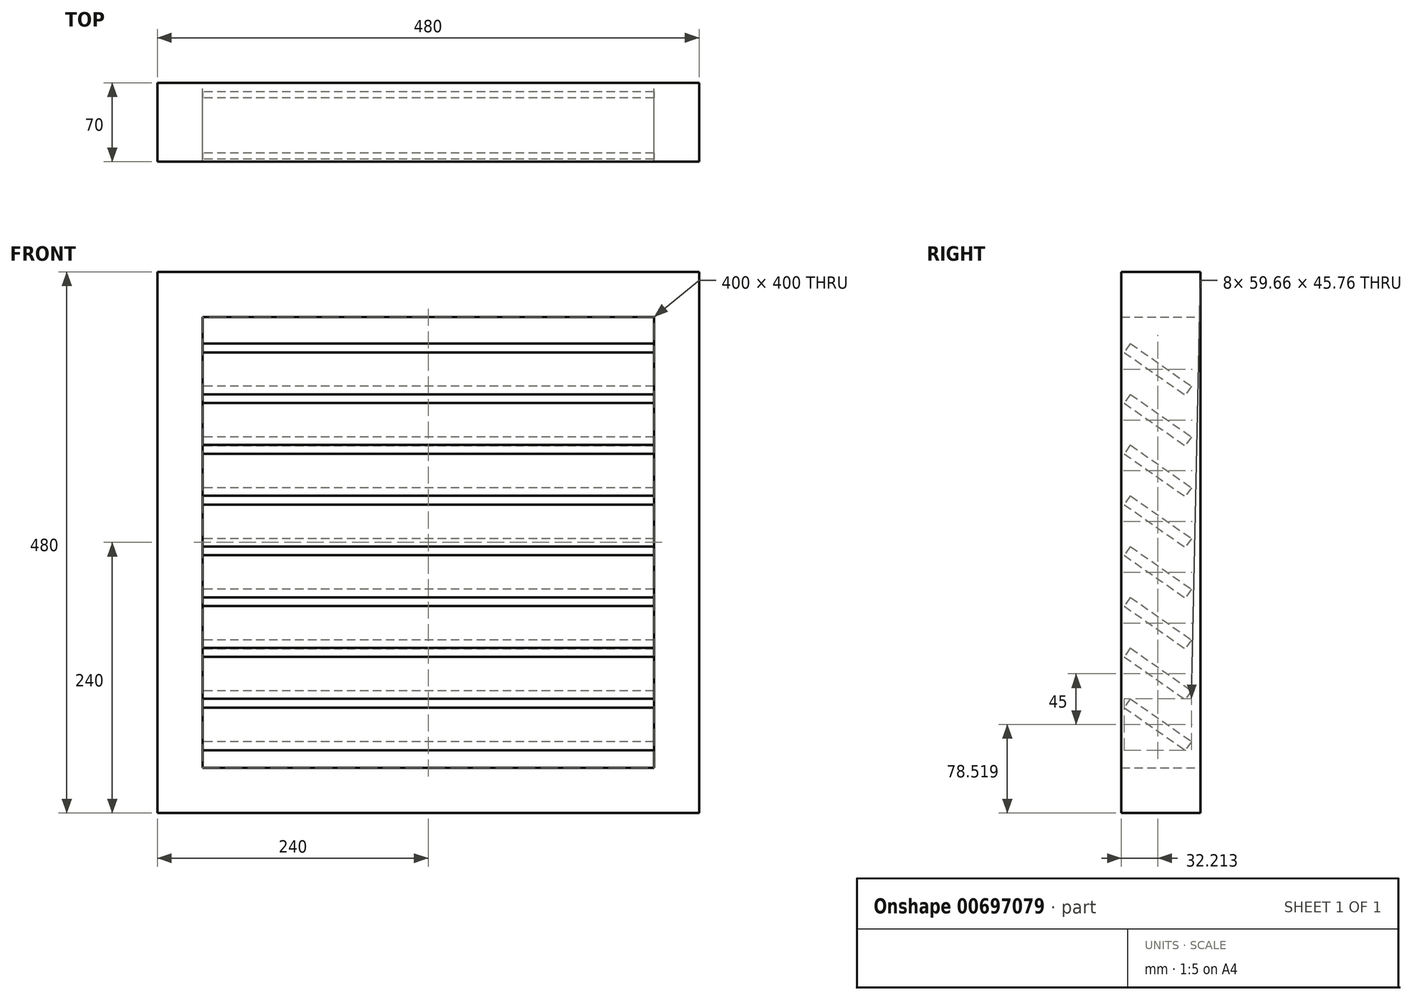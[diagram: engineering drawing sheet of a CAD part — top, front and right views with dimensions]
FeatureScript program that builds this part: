
annotation { "Feature Type Name" : "Feature", "Feature Type Description" : "" }
export const myFeature = defineFeature(function(context is Context, id is Id, definition is map)
    precondition{}
    {
        {
            var Q0;
            Q0=qCreatedBy(makeId("Front.planeOp"),FACE);
            var sketch = newSketch(context, id + "F0", { "sketchPlane" : qUnion([Q0])});
            skLineSegment(sketch, "E0.bottom", {"start": v(-200, 200) * mm, "end": v(200, 200) * mm});
            skLineSegment(sketch, "E0.top", {"start": v(-200, -200) * mm, "end": v(200, -200) * mm});
            skLineSegment(sketch, "E0.left", {"start": v(-200, 200) * mm, "end": v(-200, -200) * mm});
            skLineSegment(sketch, "E0.right", {"start": v(200, 200) * mm, "end": v(200, -200) * mm});
            skLineSegment(sketch, "E1", {"start": v(-286.4, 0) * mm, "end": v(373.23, 0) * mm, "construction": true});
            skLineSegment(sketch, "E2", {"start": v(0, 313.1) * mm, "end": v(0, -326.9) * mm, "construction": true});
            skLineSegment(sketch, "E3.0", {"start": v(240, 240) * mm, "end": v(240, -240) * mm});
            skLineSegment(sketch, "E3.1", {"start": v(-240, 240) * mm, "end": v(240, 240) * mm});
            skLineSegment(sketch, "E3.2", {"start": v(-240, 240) * mm, "end": v(-240, -240) * mm});
            skLineSegment(sketch, "E3.3", {"start": v(-240, -240) * mm, "end": v(240, -240) * mm});
            skSolve(sketch);
        }
        {
            var Q0;
            Q0=makeQuery(id+"F0.imprint","IMPRINT",FACE,{"disambiguationData":[TD([[makeQuery(id+"F0.imprint","IMPRINT",EDGE,{"derivedFrom":sQuery(id+"F0.wireOp",EDGE,"E0.bottom")}),1.0]])]});
            extrude(context, id + "F1", {"entities" : qUnion([Q0]), "depth" : 70 * mm, "offsetDistance" : 25 * mm});
        }
        {
            var Q0;
            Q0=makeQuery(id+"F1.opExtrude","SWEPT_FACE",FACE,{"disambiguationData":[OSD([sQuery(id+"F0.wireOp",EDGE,"E0.left")])]});
            var sketch = newSketch(context, id + "F2", { "sketchPlane" : qUnion([Q0])});
            skLineSegment(sketch, "E4", {"start": v(-95.23, 71.49) * mm, "end": v(-32.08, 271.77) * mm, "construction": true});
            skLineSegment(sketch, "E5", {"start": v(-95.23, 71.49) * mm, "end": v(71.38, 199.33) * mm, "construction": true});
            skArc(sketch, "E6.trimOffspring", {"start": v(-15.9, 132.37) * mm, "mid": v(-37.87, 153.4) * mm, "end": v(-65.15, 166.86) * mm});
            skArc(sketch, "E7.trimOffspring", {"start": v(-7.96, 138.45) * mm, "mid": v(-32.13, 161.6) * mm, "end": v(-62.15, 176.4) * mm});
            skArc(sketch, "E8", {"start": v(-15.9, 132.37) * mm, "mid": v(-8.88, 131.44) * mm, "end": v(-7.96, 138.45) * mm});
            skArc(sketch, "E9", {"start": v(-62.15, 176.4) * mm, "mid": v(-68.42, 173.13) * mm, "end": v(-65.15, 166.86) * mm});
            skLineSegment(sketch, "E10", {"start": v(-35, 71.49) * mm, "end": v(-95.23, 71.49) * mm, "construction": true});
            skLineSegment(sketch, "E11.0", {"start": v(-70, 200) * mm, "end": v(0, 200) * mm, "construction": true});
            skLineSegment(sketch, "E12.0", {"start": v(-70, 200) * mm, "end": v(-70, -200) * mm, "construction": true});
            skArc(sketch, "E13", {"start": v(-11.92, 135.4) * mm, "mid": v(-35, 157.5) * mm, "end": v(-63.65, 171.63) * mm, "construction": true});
            skLineSegment(sketch, "E14", {"start": v(-95.23, 71.49) * mm, "end": v(25.23, 243.51) * mm, "construction": true});
            skPoint(sketch, "E15", {"position": v(-35, 157.5) * mm});
            skLineSegment(sketch, "E16", {"start": v(-35, 157.5) * mm, "end": v(-35, 71.49) * mm, "construction": true});
            skArc(sketch, "E17.0.1.0", {"start": v(-15.9, 87.37) * mm, "mid": v(-37.87, 108.4) * mm, "end": v(-65.15, 121.86) * mm});
            skArc(sketch, "E17.0.1.1", {"start": v(-11.92, 90.4) * mm, "mid": v(-35, 112.5) * mm, "end": v(-63.65, 126.63) * mm, "construction": true});
            skArc(sketch, "E17.0.1.2", {"start": v(-15.9, 87.37) * mm, "mid": v(-8.88, 86.44) * mm, "end": v(-7.96, 93.45) * mm});
            skArc(sketch, "E17.0.1.3", {"start": v(-7.96, 93.45) * mm, "mid": v(-32.13, 116.6) * mm, "end": v(-62.15, 131.4) * mm});
            skArc(sketch, "E17.0.1.4", {"start": v(-62.15, 131.4) * mm, "mid": v(-68.42, 128.13) * mm, "end": v(-65.15, 121.86) * mm});
            skArc(sketch, "E17.0.2.0", {"start": v(-15.9, 42.37) * mm, "mid": v(-37.87, 63.4) * mm, "end": v(-65.15, 76.86) * mm});
            skArc(sketch, "E17.0.2.1", {"start": v(-11.92, 45.4) * mm, "mid": v(-35, 67.5) * mm, "end": v(-63.65, 81.63) * mm, "construction": true});
            skArc(sketch, "E17.0.2.2", {"start": v(-15.9, 42.37) * mm, "mid": v(-8.88, 41.44) * mm, "end": v(-7.96, 48.45) * mm});
            skArc(sketch, "E17.0.2.3", {"start": v(-7.96, 48.45) * mm, "mid": v(-32.13, 71.6) * mm, "end": v(-62.15, 86.4) * mm});
            skArc(sketch, "E17.0.2.4", {"start": v(-62.15, 86.4) * mm, "mid": v(-68.42, 83.13) * mm, "end": v(-65.15, 76.86) * mm});
            skArc(sketch, "E17.0.3.0", {"start": v(-15.9, -2.63) * mm, "mid": v(-37.87, 18.4) * mm, "end": v(-65.15, 31.86) * mm});
            skArc(sketch, "E17.0.3.1", {"start": v(-11.92, 0.4) * mm, "mid": v(-35, 22.5) * mm, "end": v(-63.65, 36.63) * mm, "construction": true});
            skArc(sketch, "E17.0.3.2", {"start": v(-15.9, -2.63) * mm, "mid": v(-8.88, -3.56) * mm, "end": v(-7.96, 3.45) * mm});
            skArc(sketch, "E17.0.3.3", {"start": v(-7.96, 3.45) * mm, "mid": v(-32.13, 26.6) * mm, "end": v(-62.15, 41.4) * mm});
            skArc(sketch, "E17.0.3.4", {"start": v(-62.15, 41.4) * mm, "mid": v(-68.42, 38.13) * mm, "end": v(-65.15, 31.86) * mm});
            skArc(sketch, "E17.0.4.0", {"start": v(-15.9, -47.63) * mm, "mid": v(-37.87, -26.6) * mm, "end": v(-65.15, -13.14) * mm});
            skArc(sketch, "E17.0.4.1", {"start": v(-11.92, -44.6) * mm, "mid": v(-35, -22.5) * mm, "end": v(-63.65, -8.37) * mm, "construction": true});
            skArc(sketch, "E17.0.4.2", {"start": v(-15.9, -47.63) * mm, "mid": v(-8.88, -48.56) * mm, "end": v(-7.96, -41.55) * mm});
            skArc(sketch, "E17.0.4.3", {"start": v(-7.96, -41.55) * mm, "mid": v(-32.13, -18.4) * mm, "end": v(-62.15, -3.6) * mm});
            skArc(sketch, "E17.0.4.4", {"start": v(-62.15, -3.6) * mm, "mid": v(-68.42, -6.87) * mm, "end": v(-65.15, -13.14) * mm});
            skArc(sketch, "E17.0.5.0", {"start": v(-15.9, -92.63) * mm, "mid": v(-37.87, -71.6) * mm, "end": v(-65.15, -58.14) * mm});
            skArc(sketch, "E17.0.5.1", {"start": v(-11.92, -89.6) * mm, "mid": v(-35, -67.5) * mm, "end": v(-63.65, -53.37) * mm, "construction": true});
            skArc(sketch, "E17.0.5.2", {"start": v(-15.9, -92.63) * mm, "mid": v(-8.88, -93.56) * mm, "end": v(-7.96, -86.55) * mm});
            skArc(sketch, "E17.0.5.3", {"start": v(-7.96, -86.55) * mm, "mid": v(-32.13, -63.4) * mm, "end": v(-62.15, -48.6) * mm});
            skArc(sketch, "E17.0.5.4", {"start": v(-62.15, -48.6) * mm, "mid": v(-68.42, -51.87) * mm, "end": v(-65.15, -58.14) * mm});
            skArc(sketch, "E17.0.6.0", {"start": v(-15.9, -137.63) * mm, "mid": v(-37.87, -116.6) * mm, "end": v(-65.15, -103.14) * mm});
            skArc(sketch, "E17.0.6.1", {"start": v(-11.92, -134.6) * mm, "mid": v(-35, -112.5) * mm, "end": v(-63.65, -98.37) * mm, "construction": true});
            skArc(sketch, "E17.0.6.2", {"start": v(-15.9, -137.63) * mm, "mid": v(-8.88, -138.56) * mm, "end": v(-7.96, -131.55) * mm});
            skArc(sketch, "E17.0.6.3", {"start": v(-7.96, -131.55) * mm, "mid": v(-32.13, -108.4) * mm, "end": v(-62.15, -93.6) * mm});
            skArc(sketch, "E17.0.6.4", {"start": v(-62.15, -93.6) * mm, "mid": v(-68.42, -96.87) * mm, "end": v(-65.15, -103.14) * mm});
            skArc(sketch, "E17.0.7.0", {"start": v(-15.9, -182.63) * mm, "mid": v(-37.87, -161.6) * mm, "end": v(-65.15, -148.14) * mm});
            skArc(sketch, "E17.0.7.1", {"start": v(-11.92, -179.6) * mm, "mid": v(-35, -157.5) * mm, "end": v(-63.65, -143.37) * mm, "construction": true});
            skArc(sketch, "E17.0.7.2", {"start": v(-15.9, -182.63) * mm, "mid": v(-8.88, -183.56) * mm, "end": v(-7.96, -176.55) * mm});
            skArc(sketch, "E17.0.7.3", {"start": v(-7.96, -176.55) * mm, "mid": v(-32.13, -153.4) * mm, "end": v(-62.15, -138.6) * mm});
            skArc(sketch, "E17.0.7.4", {"start": v(-62.15, -138.6) * mm, "mid": v(-68.42, -141.87) * mm, "end": v(-65.15, -148.14) * mm});
            skLineSegment(sketch, "E17.direction1", {"start": v(-95.23, 71.49) * mm, "end": v(-70.23, 71.49) * mm, "construction": true});
            skLineSegment(sketch, "E17.direction2", {"start": v(-95.23, 71.49) * mm, "end": v(-95.23, 26.49) * mm, "construction": true});
            skLineSegment(sketch, "E18", {"start": v(-35, -200) * mm, "end": v(-35, -137.94) * mm, "construction": true});
            skPoint(sketch, "E19", {"position": v(-35, -157.5) * mm});
            skSolve(sketch);
        }
        {
            var Q0;
            Q0=makeQuery(id+"F1.opExtrude","SWEPT_FACE",FACE,{"disambiguationData":[OSD([sQuery(id+"F0.wireOp",EDGE,"E0.left")])]});
            var sketch = newSketch(context, id + "F3", { "sketchPlane" : qUnion([Q0])});
            skLineSegment(sketch, "E20", {"start": v(-95.23, 71.49) * mm, "end": v(-32.08, 271.77) * mm, "construction": true});
            skLineSegment(sketch, "E21", {"start": v(-95.23, 71.49) * mm, "end": v(71.38, 199.33) * mm, "construction": true});
            skArc(sketch, "E22.trimOffspring", {"start": v(-15.9, 132.37) * mm, "mid": v(-37.87, 153.4) * mm, "end": v(-65.15, 166.86) * mm, "construction": true});
            skArc(sketch, "E23.trimOffspring", {"start": v(-7.96, 138.45) * mm, "mid": v(-32.13, 161.6) * mm, "end": v(-62.15, 176.4) * mm, "construction": true});
            skArc(sketch, "E24", {"start": v(-15.9, 132.37) * mm, "mid": v(-8.88, 131.44) * mm, "end": v(-7.96, 138.45) * mm, "construction": true});
            skArc(sketch, "E25", {"start": v(-62.15, 176.4) * mm, "mid": v(-68.42, 173.13) * mm, "end": v(-65.15, 166.86) * mm, "construction": true});
            skLineSegment(sketch, "E26", {"start": v(-35, 71.49) * mm, "end": v(-95.23, 71.49) * mm, "construction": true});
            skLineSegment(sketch, "E27.0", {"start": v(-70, 200) * mm, "end": v(39.9, 200) * mm, "construction": true});
            skLineSegment(sketch, "E28.0", {"start": v(-70, 200) * mm, "end": v(-70, -200) * mm, "construction": true});
            skArc(sketch, "E29", {"start": v(-11.92, 135.4) * mm, "mid": v(-35, 157.5) * mm, "end": v(-63.65, 171.63) * mm, "construction": true});
            skLineSegment(sketch, "E30", {"start": v(-95.23, 71.49) * mm, "end": v(25.23, 243.51) * mm, "construction": true});
            skPoint(sketch, "E31", {"position": v(-35, 157.5) * mm});
            skLineSegment(sketch, "E32", {"start": v(-35, 157.5) * mm, "end": v(-35, 71.49) * mm, "construction": true});
            skLineSegment(sketch, "E33.direction1", {"start": v(-95.23, 71.49) * mm, "end": v(8.91, 71.49) * mm, "construction": true});
            skLineSegment(sketch, "E34", {"start": v(-62.15, 176.4) * mm, "end": v(-7.96, 138.45) * mm});
            skLineSegment(sketch, "E35", {"start": v(-62.15, 176.4) * mm, "end": v(-67.62, 168.59) * mm});
            skLineSegment(sketch, "E36", {"start": v(-7.96, 138.45) * mm, "end": v(-13.43, 130.64) * mm});
            skLineSegment(sketch, "E37", {"start": v(-67.62, 168.59) * mm, "end": v(-13.43, 130.64) * mm});
            skLineSegment(sketch, "E38.0.1.0", {"start": v(-67.62, 123.59) * mm, "end": v(-13.43, 85.64) * mm});
            skLineSegment(sketch, "E38.0.1.1", {"start": v(-7.96, 93.45) * mm, "end": v(-13.43, 85.64) * mm});
            skLineSegment(sketch, "E38.0.1.2", {"start": v(-62.15, 131.4) * mm, "end": v(-7.96, 93.45) * mm});
            skLineSegment(sketch, "E38.0.1.3", {"start": v(-62.15, 131.4) * mm, "end": v(-67.62, 123.59) * mm});
            skLineSegment(sketch, "E38.0.2.0", {"start": v(-67.62, 78.59) * mm, "end": v(-13.43, 40.64) * mm});
            skLineSegment(sketch, "E38.0.2.1", {"start": v(-7.96, 48.45) * mm, "end": v(-13.43, 40.64) * mm});
            skLineSegment(sketch, "E38.0.2.2", {"start": v(-62.15, 86.4) * mm, "end": v(-7.96, 48.45) * mm});
            skLineSegment(sketch, "E38.0.2.3", {"start": v(-62.15, 86.4) * mm, "end": v(-67.62, 78.59) * mm});
            skLineSegment(sketch, "E38.0.3.0", {"start": v(-67.62, 33.59) * mm, "end": v(-13.43, -4.36) * mm});
            skLineSegment(sketch, "E38.0.3.1", {"start": v(-7.96, 3.45) * mm, "end": v(-13.43, -4.36) * mm});
            skLineSegment(sketch, "E38.0.3.2", {"start": v(-62.15, 41.4) * mm, "end": v(-7.96, 3.45) * mm});
            skLineSegment(sketch, "E38.0.3.3", {"start": v(-62.15, 41.4) * mm, "end": v(-67.62, 33.59) * mm});
            skLineSegment(sketch, "E38.0.4.0", {"start": v(-67.62, -11.41) * mm, "end": v(-13.43, -49.36) * mm});
            skLineSegment(sketch, "E38.0.4.1", {"start": v(-7.96, -41.55) * mm, "end": v(-13.43, -49.36) * mm});
            skLineSegment(sketch, "E38.0.4.2", {"start": v(-62.15, -3.6) * mm, "end": v(-7.96, -41.55) * mm});
            skLineSegment(sketch, "E38.0.4.3", {"start": v(-62.15, -3.6) * mm, "end": v(-67.62, -11.41) * mm});
            skLineSegment(sketch, "E38.0.5.0", {"start": v(-67.62, -56.41) * mm, "end": v(-13.43, -94.36) * mm});
            skLineSegment(sketch, "E38.0.5.1", {"start": v(-7.96, -86.55) * mm, "end": v(-13.43, -94.36) * mm});
            skLineSegment(sketch, "E38.0.5.2", {"start": v(-62.15, -48.6) * mm, "end": v(-7.96, -86.55) * mm});
            skLineSegment(sketch, "E38.0.5.3", {"start": v(-62.15, -48.6) * mm, "end": v(-67.62, -56.41) * mm});
            skLineSegment(sketch, "E38.0.6.0", {"start": v(-67.62, -101.41) * mm, "end": v(-13.43, -139.36) * mm});
            skLineSegment(sketch, "E38.0.6.1", {"start": v(-7.96, -131.55) * mm, "end": v(-13.43, -139.36) * mm});
            skLineSegment(sketch, "E38.0.6.2", {"start": v(-62.15, -93.6) * mm, "end": v(-7.96, -131.55) * mm});
            skLineSegment(sketch, "E38.0.6.3", {"start": v(-62.15, -93.6) * mm, "end": v(-67.62, -101.41) * mm});
            skLineSegment(sketch, "E38.0.7.0", {"start": v(-67.62, -146.41) * mm, "end": v(-13.43, -184.36) * mm});
            skLineSegment(sketch, "E38.0.7.1", {"start": v(-7.96, -176.55) * mm, "end": v(-13.43, -184.36) * mm});
            skLineSegment(sketch, "E38.0.7.2", {"start": v(-62.15, -138.6) * mm, "end": v(-7.96, -176.55) * mm});
            skLineSegment(sketch, "E38.0.7.3", {"start": v(-62.15, -138.6) * mm, "end": v(-67.62, -146.41) * mm});
            skLineSegment(sketch, "E38.direction1", {"start": v(-67.62, 168.59) * mm, "end": v(-42.62, 168.59) * mm, "construction": true});
            skLineSegment(sketch, "E38.direction2", {"start": v(-67.62, 168.59) * mm, "end": v(-67.62, 123.59) * mm, "construction": true});
            skSolve(sketch);
        }
        {
            var Q0;
            Q0 = qSketchRegion(id + "F3", true);
            var Q1;
            Q1=makeQuery(id+"F1.opExtrude","SWEPT_FACE",FACE,{"disambiguationData":[OSD([sQuery(id+"F0.wireOp",EDGE,"E0.right")])]});
            extrude(context, id + "F4", {"entities" : qUnion([Q0]), "operationType" : NewBodyOperationType.ADD, "endBound" : BoundingType.UP_TO_SURFACE, "depth" : 25 * mm, "endBoundEntityFace" : qUnion([Q1]), "offsetDistance" : 25 * mm});
        }
    });
